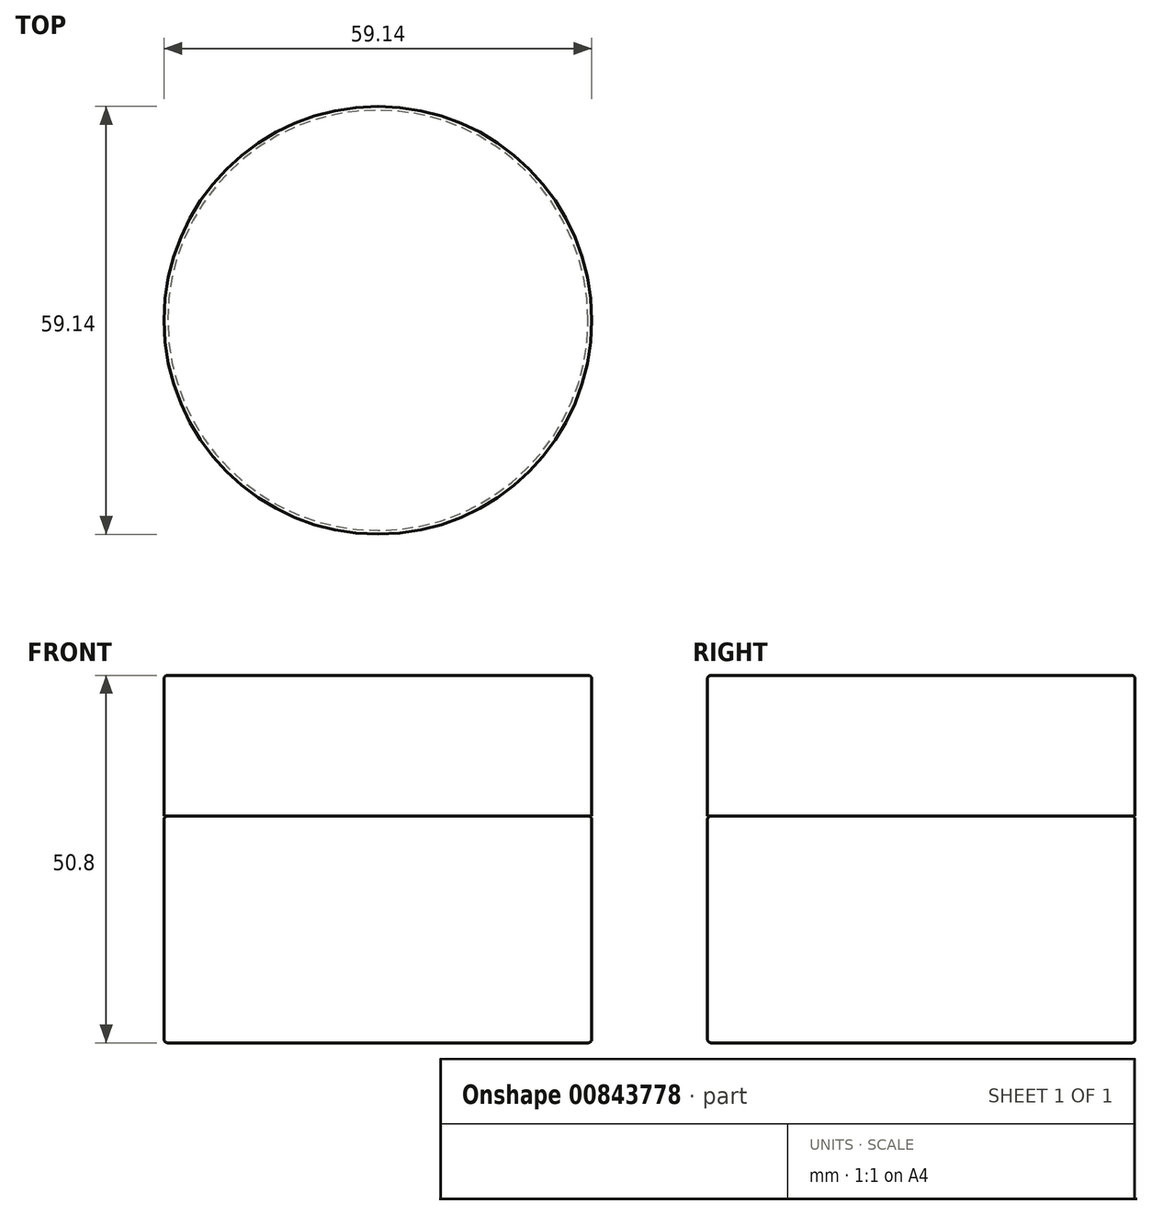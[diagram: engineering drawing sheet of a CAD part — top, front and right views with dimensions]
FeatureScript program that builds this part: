
annotation { "Feature Type Name" : "Feature", "Feature Type Description" : "" }
export const myFeature = defineFeature(function(context is Context, id is Id, definition is map)
    precondition{}
    {
        {
            var Q0;
            Q0=qCreatedBy(makeId("Top.planeOp"),FACE);
            var sketch = newSketch(context, id + "F0", { "sketchPlane" : qUnion([Q0])});
            skCircle(sketch, "E0", {"center": v(0, 0) * mm, "radius": 29.57 * mm});
            skSolve(sketch);
        }
        {
            var Q0;
            Q0=makeQuery(id+"F0.imprint","IMPRINT",FACE,{"disambiguationData":[TD([[makeQuery(id+"F0.imprint","IMPRINT",EDGE,{"derivedFrom":sQuery(id+"F0.wireOp",EDGE,"E0")}),1.0]])]});
            var Q1;
            Q1=sQuery(id+"F0.wireOp",EDGE,"E0");
            extrude(context, id + "F1", {"entities" : qUnion([Q0]), "surfaceEntities" : qUnion([Q1]), "depth" : 31.35 * mm, "offsetDistance" : 25.4 * mm});
        }
        {
            var Q0;
            Q0=makeQuery(id+"F1.opExtrude","CAP_EDGE",EDGE,{"disambiguationData":[OSD([sQuery(id+"F0.wireOp",EDGE,"E0")])],"isStart":true});
            var Q1;
            Q1=makeQuery(id+"F1.opExtrude","CAP_EDGE",EDGE,{"disambiguationData":[OSD([sQuery(id+"F0.wireOp",EDGE,"E0")])],"isStart":false});
            fillet(context, id + "F2", {"entities" : qUnion([Q0, Q1]), "radius" : 0.5 * mm, "tangentPropagation" : true, "allowEdgeOverflow" : false});
        }
        {
            var Q0;
            Q0=makeQuery(id+"F1.opExtrude","CAP_FACE",FACE,{"disambiguationData":[OSD([sQuery(id+"F0.wireOp",EDGE,"E0")])],"isStart":false});
            var sketch = newSketch(context, id + "F3", { "sketchPlane" : qUnion([Q0])});
            skCircle(sketch, "E1", {"center": v(0, 0) * mm, "radius": 29.57 * mm});
            skSolve(sketch);
        }
        {
            var Q0;
            Q0 = qSketchRegion(id + "F3", true);
            var Q1;
            Q1=sQuery(id+"F3.wireOp",EDGE,"E1");
            extrude(context, id + "F4", {"entities" : qUnion([Q0]), "operationType" : NewBodyOperationType.ADD, "surfaceEntities" : qUnion([Q1]), "depth" : 19.45 * mm, "offsetDistance" : 25.4 * mm});
        }
        {
            var Q0;
            Q0=makeQuery(id+"F4.opExtrude","CAP_EDGE",EDGE,{"disambiguationData":[OSD([sQuery(id+"F3.wireOp",EDGE,"E1")])],"isStart":false});
            fillet(context, id + "F5", {"entities" : qUnion([Q0]), "radius" : 0.5 * mm, "tangentPropagation" : true, "allowEdgeOverflow" : false});
        }
    });
